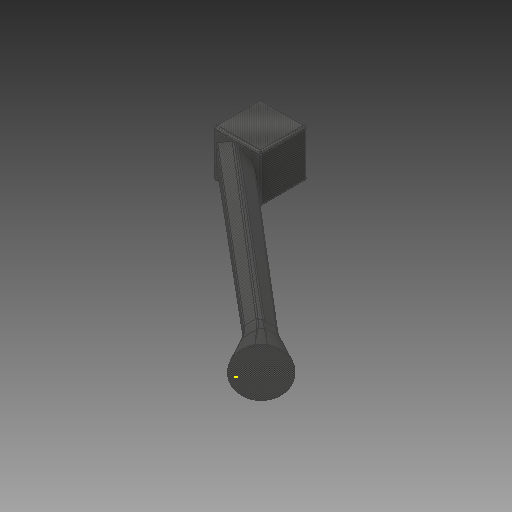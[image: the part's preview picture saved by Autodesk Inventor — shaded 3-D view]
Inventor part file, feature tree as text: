
AUTODESK INVENTOR PART (.ipt)
format: ipt  version: 2018 (Build 220112000, 112)  size: 1,882,112 bytes
history: native  units: mm
features: fillet x22, sketch x11, plane x6, loft x4, chamfer x3, other x3, extrude x2
ambient origin geometry x8: Origin, YZ Plane, XZ Plane, XY Plane, X Axis, Y Axis, Z Axis, Center Point
bodies: Solid1 (feature_tree)
feature tree (51):
  extrude  "Extrusion1"  Depth=100.0mm
  extrude  "Extrusion2"  Depth=50.0mm
  fillet  "Fillet1"  Radius=20.0mm
  fillet  "Fillet2"  Radius=2.0mm
  fillet  "Fillet3"  Radius=5.0mm
  fillet  "Fillet4"  Radius=5.0mm
  fillet  "Fillet5"  Radius=5.0mm
  chamfer  "Chamfer1"  Distance=2.0mm Angle=45.0deg
  fillet  "Fillet6"  Radius=4.0mm
  fillet  "Fillet7"  Radius=2.0mm
  sketch  "Sketch3"  dims[d11=5.0mm d12=2.0mm d13=2.0mm d14=45.0deg d15=4.0mm d16=2.0mm]
  plane  "Work Plane1"
  plane  "Work Plane2"
  plane  "Work Plane4"
  loft  "Loft3"
  plane  "Work Plane5"
  loft  "Loft4"
  fillet  "Fillet24"  Radius=5.0mm
  fillet  "Fillet25"  Radius=10.0mm
  fillet  "Fillet26"  Radius=20.0mm
  fillet  "Fillet27"  Radius=50.0mm
  fillet  "Fillet28"  Radius=25.0mm
  fillet  "Fillet29"  Radius=25.0mm
  fillet  "Fillet30"  [1 undecoded]
  fillet  "Fillet31"  [1 undecoded]
  fillet  "Fillet32"  Radius=80.0mm
  fillet  "Fillet33"  Radius=100.0mm
  fillet  "Fillet34"  [1 undecoded]
  fillet  "Fillet35"  [1 undecoded]
  fillet  "Fillet36"  Radius=100.0mm
  chamfer  "Chamfer2"  Distance=100.0mm
  chamfer  "Chamfer3"  Distance=5.0mm
  fillet  "Fillet37"  Radius=5.0mm
  sketch  "Sketch10"  dims[d75=100.0mm]
  plane  "Work Plane6"
  sketch  "Sketch11"  dims[d76=100.0mm]
  sketch  "Sketch12"  dims[d77=100.0mm]
  loft  "Loft5"
  plane  "Work Plane7"
  sketch  "Sketch14"  dims[d79=100.0mm]
  loft  "Loft6"
  fillet  "Fillet38"  Radius=5.0mm
  sketch  "Sketch1"  dims[d0=100.0mm d1=100.0mm]
  sketch  "Sketch2"  dims[d2=100.0mm d3=0.0mm d4=50.0mm d5=20.0mm d6=0.0mm d7=2.0mm d8=5.0mm d9=5.0mm d10=5.0mm]
  sketch  "Sketch8"  dims[d20=10.0mm d21=40.0mm]
  sketch  "Sketch9"  dims[d22=40.0mm d23=45.0deg d24=260.0mm d57=420.0mm d58=5.0mm d59=10.0mm d60=20.0mm d61=50.0mm d62=25.0mm d63=25.0mm d64=0.0mm d65=90.0deg d66=0.0mm d67=90.0deg d68=80.0mm d69=100.0mm d70=0.0mm d71=90.0deg d72=0.0mm d73=90.0deg d74=100.0mm]
  other  "Edges2"
  sketch  "Sketch13"  dims[d78=100.0mm]
  other  "Edges3"
  sketch  "Sketch15"  dims[d80=100.0mm d81=100.0mm d82=5.0mm d83=5.0mm d84=5.0mm d85=5.0mm d86=5.0mm d87=2.0mm d88=2.0mm d89=45.0deg d90=2.0mm d91=2.0mm d92=45.0deg d93=5.0mm d94=3.0mm d95=52.5mm d96=100.0mm d97=0.0mm d98=90.0deg d99=0.0mm d100=90.0deg d101=1.0mm d102=100.0mm d103=0.0mm d104=90.0deg d105=0.0mm d106=90.0deg d107=5.0mm]
  other  "Edges4"
note: 4 required parameter values undecoded (feature->parameter linkage not recoverable at this tier; creation-order binding heuristic only, values carry confidence <= 0.55)
